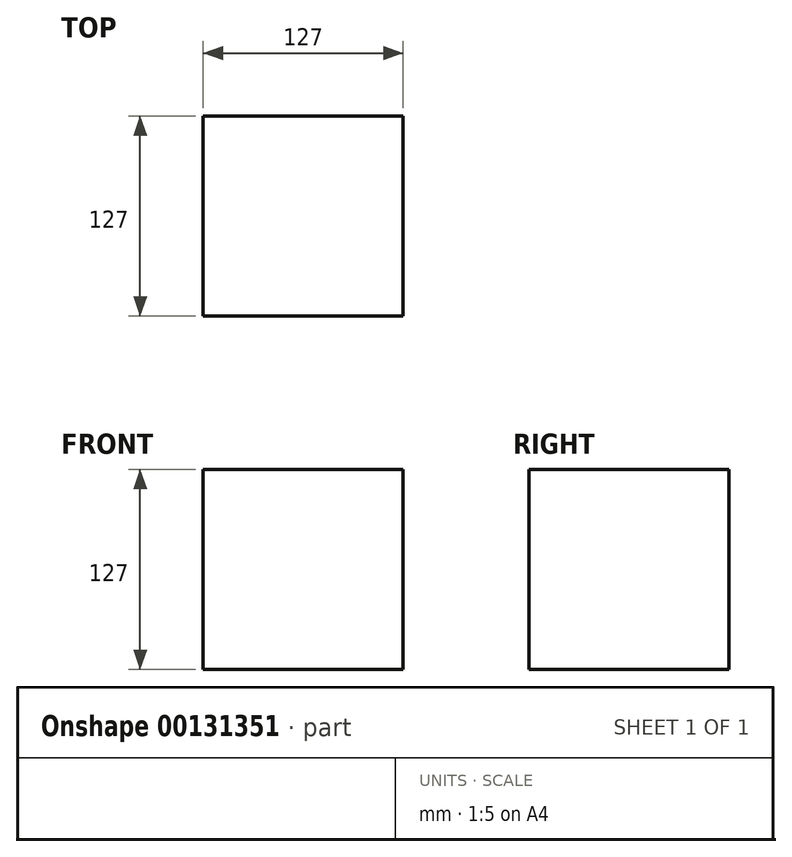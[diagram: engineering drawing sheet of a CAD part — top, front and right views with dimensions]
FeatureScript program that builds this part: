
annotation { "Feature Type Name" : "Feature", "Feature Type Description" : "" }
export const myFeature = defineFeature(function(context is Context, id is Id, definition is map)
    precondition{}
    {
        {
            var Q0;
            Q0=qCreatedBy(makeId("Front.planeOp"),FACE);
            var sketch = newSketch(context, id + "F0", { "sketchPlane" : qUnion([Q0])});
            skLineSegment(sketch, "E0.bottom", {"start": v(-65.34, 64.12) * mm, "end": v(61.66, 64.12) * mm});
            skLineSegment(sketch, "E0.top", {"start": v(-65.34, -62.88) * mm, "end": v(61.66, -62.88) * mm});
            skLineSegment(sketch, "E0.left", {"start": v(-65.34, 64.12) * mm, "end": v(-65.34, -62.88) * mm});
            skLineSegment(sketch, "E0.right", {"start": v(61.66, 64.12) * mm, "end": v(61.66, -62.88) * mm});
            skSolve(sketch);
        }
        {
            var Q0;
            Q0 = qSketchRegion(id + "F0", true);
            extrude(context, id + "F1", {"entities" : qUnion([Q0]), "depth" : 127 * mm});
        }
    });
